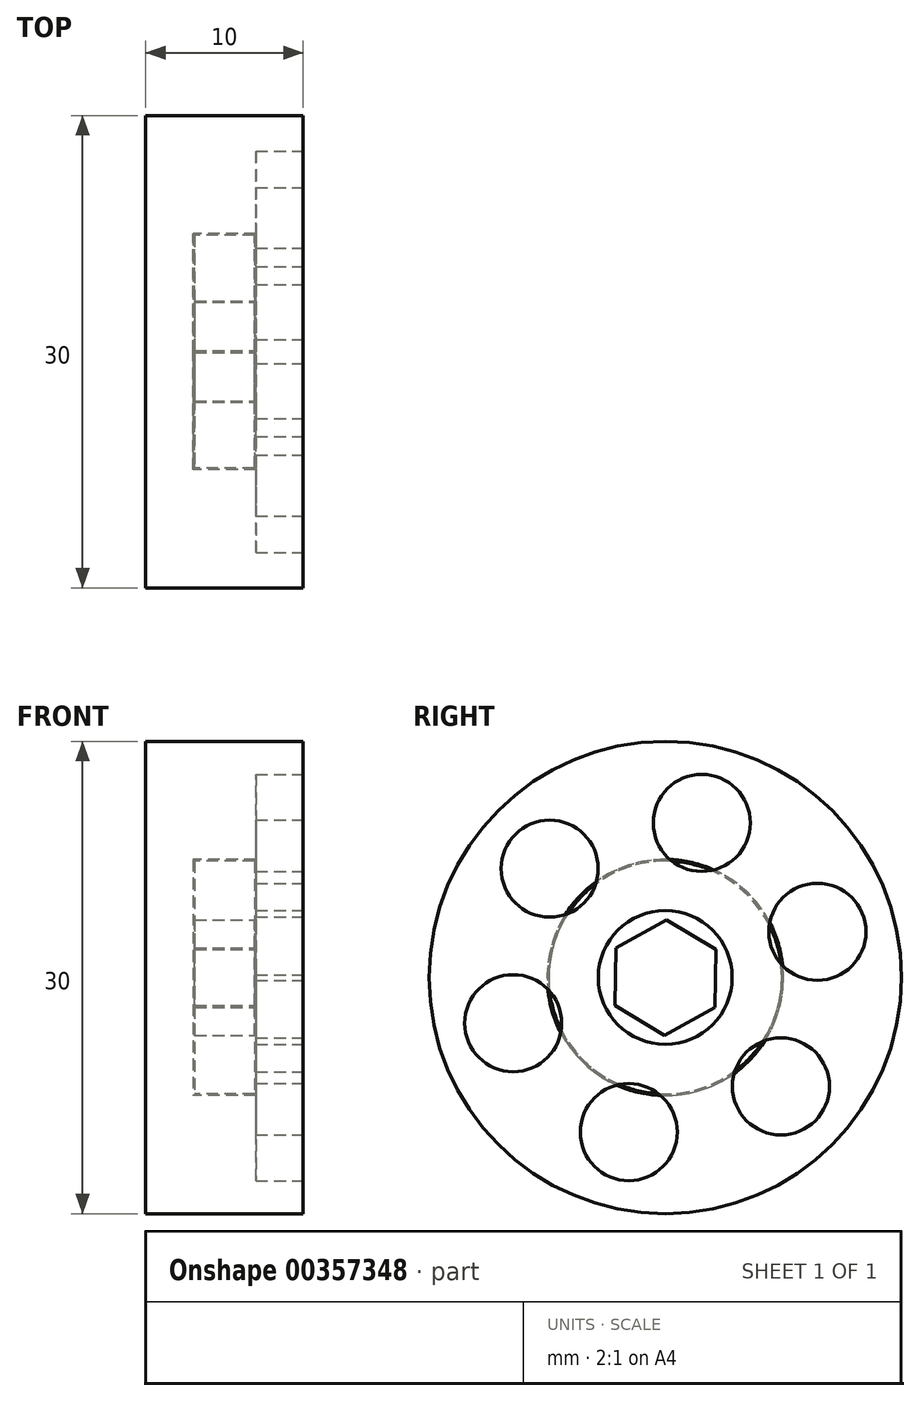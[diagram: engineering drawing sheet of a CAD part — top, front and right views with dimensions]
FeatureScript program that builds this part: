
annotation { "Feature Type Name" : "Feature", "Feature Type Description" : "" }
export const myFeature = defineFeature(function(context is Context, id is Id, definition is map)
    precondition{}
    {
        {
            var Q0;
            Q0=qCreatedBy(makeId("Front.planeOp"),FACE);
            var sketch = newSketch(context, id + "F0", { "sketchPlane" : qUnion([Q0])});
            skLineSegment(sketch, "E0.bottom", {"start": v(1.74, 0) * mm, "end": v(4.74, 0) * mm});
            skLineSegment(sketch, "E0.top", {"start": v(1.74, 15) * mm, "end": v(11.74, 15) * mm});
            skLineSegment(sketch, "E0.left", {"start": v(1.74, 0) * mm, "end": v(1.74, 15) * mm});
            skLineSegment(sketch, "E0.right", {"start": v(11.74, 0) * mm, "end": v(11.74, 15) * mm});
            skLineSegment(sketch, "E1.top", {"start": v(4.74, 7.5) * mm, "end": v(8.74, 7.5) * mm});
            skLineSegment(sketch, "E1.left", {"start": v(4.74, 0) * mm, "end": v(4.74, 7.5) * mm});
            skLineSegment(sketch, "E1.right", {"start": v(8.74, 0) * mm, "end": v(8.74, 7.5) * mm});
            skLineSegment(sketch, "E2.trimOffspring", {"start": v(8.74, 0) * mm, "end": v(11.74, 0) * mm});
            skLineSegment(sketch, "E3.bottom", {"start": v(4.84, 0) * mm, "end": v(8.64, 0) * mm});
            skLineSegment(sketch, "E3.top", {"start": v(4.84, 7.4) * mm, "end": v(8.64, 7.4) * mm});
            skLineSegment(sketch, "E3.left", {"start": v(4.84, 0) * mm, "end": v(4.84, 7.4) * mm});
            skLineSegment(sketch, "E3.right", {"start": v(8.64, 0) * mm, "end": v(8.64, 7.4) * mm});
            skLineSegment(sketch, "E4", {"start": v(-3.54, 0) * mm, "end": v(30.64, 0) * mm, "construction": true});
            skPoint(sketch, "E4.endSnap0", {"position": v(10.24, 0) * mm});
            skSolve(sketch);
        }
        {
            var Q0;
            Q0=makeQuery(id+"F0.imprint","IMPRINT",FACE,{"disambiguationData":[TD([[makeQuery(id+"F0.imprint","IMPRINT",EDGE,{"derivedFrom":sQuery(id+"F0.wireOp",EDGE,"E0.bottom")}),1.0]])]});
            var Q1;
            Q1=makeQuery(id+"F0.imprint","IMPRINT",FACE,{"disambiguationData":[TD([[makeQuery(id+"F0.imprint","IMPRINT",EDGE,{"derivedFrom":sQuery(id+"F0.wireOp",EDGE,"E3.bottom")}),1.0]])]});
            var Q2;
            Q2=sQuery(id+"F0.wireOp",EDGE,"E4");
            var Q3;
            Q3=sQuery(id+"F0.wireOp",EDGE,"E4");
            revolve(context, id + "F1", {"entities" : qUnion([Q0, Q1]), "surfaceEntities" : qUnion([Q2]), "axis" : qUnion([Q3]), "revolveType" : RevolveType.FULL});
        }
        {
            var Q0;
            Q0=makeQuery(id+"F1.opRevolve","SWEPT_FACE",FACE,{"disambiguationData":[OSD([sQuery(id+"F0.wireOp",EDGE,"E0.right")])]});
            var sketch = newSketch(context, id + "F2", { "sketchPlane" : qUnion([Q0])});
            skCircle(sketch, "E5", {"center": v(0, 0) * mm, "radius": 4.25 * mm});
            skSolve(sketch);
        }
        {
            var Q0;
            Q0=makeQuery(id+"F2.imprint","IMPRINT",FACE,{"disambiguationData":[TD([[makeQuery(id+"F2.imprint","IMPRINT",EDGE,{"derivedFrom":sQuery(id+"F2.wireOp",EDGE,"E5")}),1.0]])]});
            extrude(context, id + "F3", {"entities" : qUnion([Q0]), "operationType" : NewBodyOperationType.REMOVE, "oppositeDirection" : true, "depth" : 3 * mm});
        }
        {
            var Q0;
            Q0=makeQuery(id+"F1.opRevolve","SWEPT_FACE",FACE,{"disambiguationData":[OSD([sQuery(id+"F0.wireOp",EDGE,"E3.right")])]});
            var sketch = newSketch(context, id + "F4", { "sketchPlane" : qUnion([Q0])});
            skCircle(sketch, "E6.cCircle", {"center": v(0, 0) * mm, "radius": 3.17 * mm, "construction": true});
            skLineSegment(sketch, "E6.0", {"start": v(-0.07, -3.67) * mm, "end": v(-3.2, -1.78) * mm});
            skLineSegment(sketch, "E6.1", {"start": v(-3.2, -1.78) * mm, "end": v(-3.14, 1.89) * mm});
            skLineSegment(sketch, "E6.2", {"start": v(-3.14, 1.89) * mm, "end": v(0.07, 3.67) * mm});
            skLineSegment(sketch, "E6.3", {"start": v(0.07, 3.67) * mm, "end": v(3.2, 1.78) * mm});
            skLineSegment(sketch, "E6.4", {"start": v(3.2, 1.78) * mm, "end": v(3.14, -1.89) * mm});
            skLineSegment(sketch, "E6.5", {"start": v(3.14, -1.89) * mm, "end": v(-0.07, -3.67) * mm});
            skPoint(sketch, "E6.0.midPoint", {"position": v(-1.64, -2.72) * mm});
            skSolve(sketch);
        }
        {
            var Q0;
            Q0=makeQuery(id+"F4.imprint","IMPRINT",FACE,{"disambiguationData":[TD([[makeQuery(id+"F4.imprint","IMPRINT",EDGE,{"derivedFrom":sQuery(id+"F4.wireOp",EDGE,"E6.0")}),-1.0]])]});
            extrude(context, id + "F5", {"entities" : qUnion([Q0]), "operationType" : NewBodyOperationType.REMOVE, "oppositeDirection" : true, "depth" : 3.8 * mm});
        }
        {
            var Q0;
            Q0=makeQuery(id+"F1.opRevolve","SWEPT_FACE",FACE,{"disambiguationData":[OSD([sQuery(id+"F0.wireOp",EDGE,"E0.left")])]});
            var sketch = newSketch(context, id + "F6", { "sketchPlane" : qUnion([Q0])});
            skCircle(sketch, "E7.0", {"center": v(0, 0) * mm, "radius": 4.25 * mm});
            skSolve(sketch);
        }
        {
            var Q0;
            Q0=makeQuery(id+"F2.imprint","IMPRINT",FACE,{"disambiguationData":[TD([[makeQuery(id+"F2.imprint","IMPRINT",EDGE,{"derivedFrom":sQuery(id+"F2.wireOp",EDGE,"E5")}),-1.0]])]});
            var sketch = newSketch(context, id + "F7", { "sketchPlane" : qUnion([Q0])});
            skEllipse(sketch, "E8", {"center": v(-7.35, 6.92) * mm, "majorRadius": 3.08 * mm, "minorRadius": 3.08 * mm, "majorAxis": v(0.68, -0.73)});
            skLineSegment(sketch, "E9", {"start": v(-13.98, 13.16) * mm, "end": v(0, 0) * mm, "construction": true});
            skEllipse(sketch, "E10.1.0", {"center": v(-9.66, -2.9) * mm, "majorRadius": 3.08 * mm, "minorRadius": 3.08 * mm, "majorAxis": v(0.97, 0.23)});
            skEllipse(sketch, "E10.2.0", {"center": v(-2.32, -9.82) * mm, "majorRadius": 3.08 * mm, "minorRadius": 3.08 * mm, "majorAxis": v(0.3, 0.96)});
            skEllipse(sketch, "E10.3.0", {"center": v(7.35, -6.92) * mm, "majorRadius": 3.08 * mm, "minorRadius": 3.08 * mm, "majorAxis": v(-0.68, 0.73)});
            skEllipse(sketch, "E10.4.0", {"center": v(9.66, 2.9) * mm, "majorRadius": 3.08 * mm, "minorRadius": 3.08 * mm, "majorAxis": v(-0.97, -0.23)});
            skEllipse(sketch, "E10.5.0", {"center": v(2.32, 9.82) * mm, "majorRadius": 3.08 * mm, "minorRadius": 3.08 * mm, "majorAxis": v(-0.3, -0.96)});
            skPoint(sketch, "E10.center", {"position": v(0, 0) * mm});
            skSolve(sketch);
        }
        {
            var Q0;
            Q0=makeQuery(id+"F7.imprint","IMPRINT",FACE,{"disambiguationData":[TD([[makeQuery(id+"F7.imprint","IMPRINT",EDGE,{"derivedFrom":sQuery(id+"F7.wireOp",EDGE,"E8")}),1.0]])]});
            var Q1;
            Q1=makeQuery(id+"F7.imprint","IMPRINT",FACE,{"disambiguationData":[TD([[makeQuery(id+"F7.imprint","IMPRINT",EDGE,{"derivedFrom":sQuery(id+"F7.wireOp",EDGE,"E10.5.0")}),1.0]])]});
            var Q2;
            Q2=makeQuery(id+"F7.imprint","IMPRINT",FACE,{"disambiguationData":[TD([[makeQuery(id+"F7.imprint","IMPRINT",EDGE,{"derivedFrom":sQuery(id+"F7.wireOp",EDGE,"E10.4.0")}),1.0]])]});
            var Q3;
            Q3=makeQuery(id+"F7.imprint","IMPRINT",FACE,{"disambiguationData":[TD([[makeQuery(id+"F7.imprint","IMPRINT",EDGE,{"derivedFrom":sQuery(id+"F7.wireOp",EDGE,"E10.3.0")}),1.0]])]});
            var Q4;
            Q4=makeQuery(id+"F7.imprint","IMPRINT",FACE,{"disambiguationData":[TD([[makeQuery(id+"F7.imprint","IMPRINT",EDGE,{"derivedFrom":sQuery(id+"F7.wireOp",EDGE,"E10.2.0")}),1.0]])]});
            var Q5;
            Q5=makeQuery(id+"F7.imprint","IMPRINT",FACE,{"disambiguationData":[TD([[makeQuery(id+"F7.imprint","IMPRINT",EDGE,{"derivedFrom":sQuery(id+"F7.wireOp",EDGE,"E10.1.0")}),1.0]])]});
            extrude(context, id + "F8", {"entities" : qUnion([Q0, Q1, Q2, Q3, Q4, Q5]), "operationType" : NewBodyOperationType.REMOVE, "oppositeDirection" : true, "depth" : 3 * mm});
        }
    });
